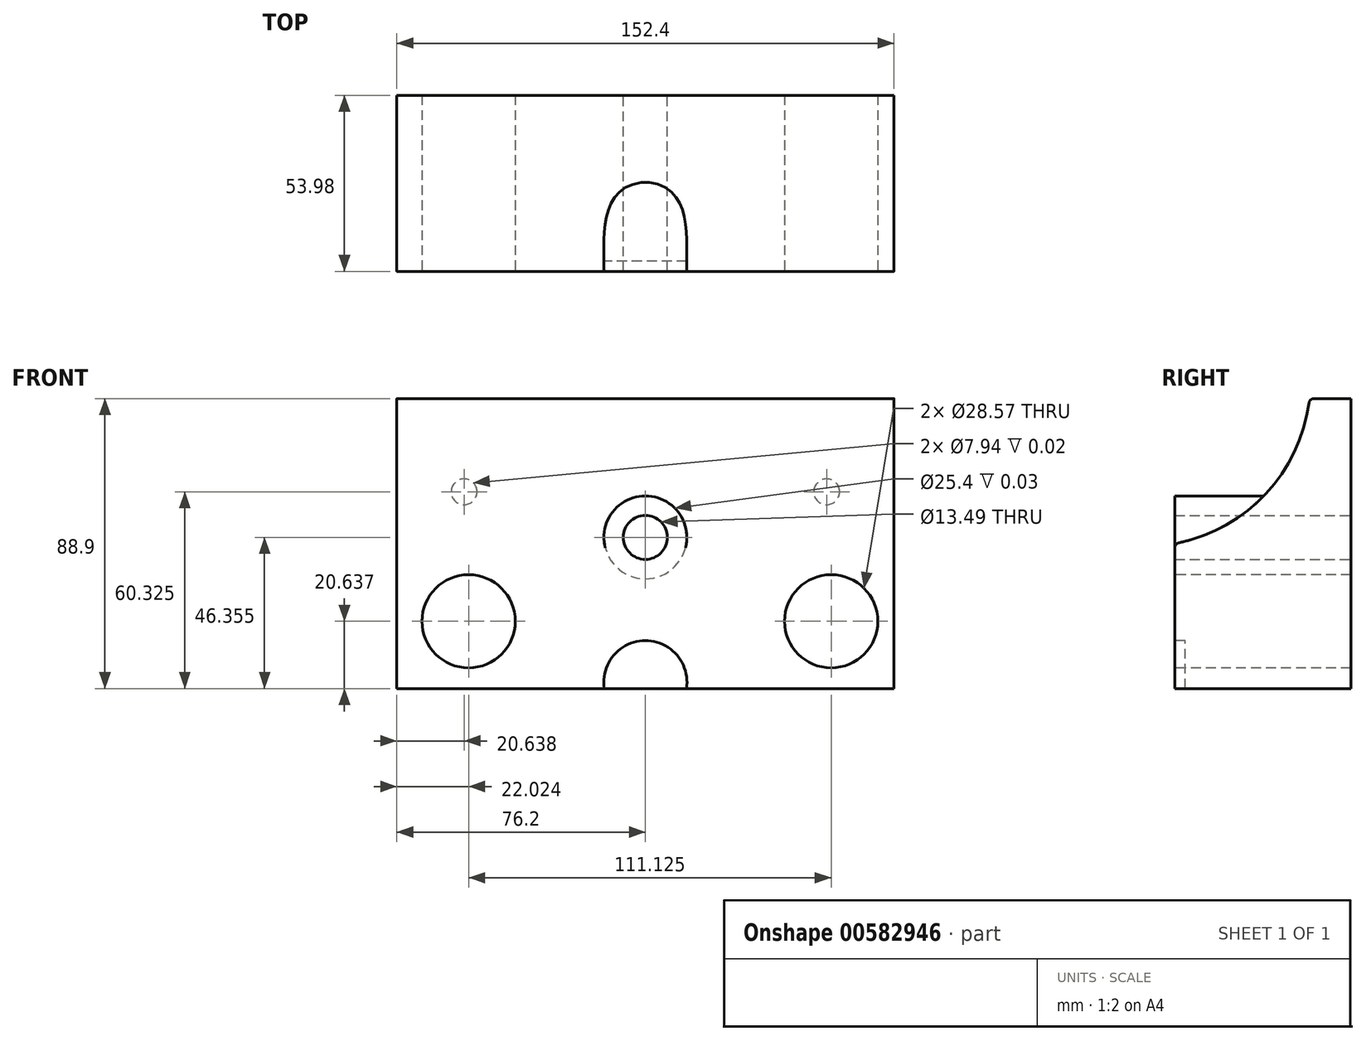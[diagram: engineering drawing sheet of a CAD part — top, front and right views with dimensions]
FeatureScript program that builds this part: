
annotation { "Feature Type Name" : "Feature", "Feature Type Description" : "" }
export const myFeature = defineFeature(function(context is Context, id is Id, definition is map)
    precondition{}
    {
        {
            var Q0;
            Q0=qCreatedBy(makeId("Right.planeOp"),FACE);
            var sketch = newSketch(context, id + "F0", { "sketchPlane" : qUnion([Q0])});
            skLineSegment(sketch, "E0.bottom", {"start": v(-53.97, 0) * mm, "end": v(0, 0) * mm});
            skLineSegment(sketch, "E0.top", {"start": v(-12.7, 88.9) * mm, "end": v(0, 88.9) * mm});
            skLineSegment(sketch, "E0.left", {"start": v(-53.97, 0) * mm, "end": v(-53.98, 44.45) * mm});
            skLineSegment(sketch, "E0.right", {"start": v(0, 0) * mm, "end": v(0, 88.9) * mm});
            skPoint(sketch, "E0.middle", {"position": v(0, 0) * mm});
            skPoint(sketch, "E1", {"position": v(-53.97, 44.45) * mm});
            skLineSegment(sketch, "E2", {"start": v(-53.97, 44.45) * mm, "end": v(-53.97, 44.45) * mm});
            skPoint(sketch, "E3.orphan", {"position": v(-53.98, 88.9) * mm});
            skPoint(sketch, "E4.visualSharp", {"position": v(-294.66, 0) * mm});
            skArc(sketch, "E4.filletArc", {"start": v(-53.97, 44.45) * mm, "mid": v(-25.97, 59.84) * mm, "end": v(-12.7, 88.9) * mm});
            skSolve(sketch);
        }
        {
            var Q0;
            {var subQ1=sQuery(id+"F0.wireOp",EDGE,"E0.bottom");Q0=makeQuery(id+"F0.imprint","IMPRINT",FACE,{"disambiguationData":[TD([[makeQuery(id+"F0.imprint","IMPRINT",EDGE,{"derivedFrom":subQ1}),1.0]])]});}
            extrude(context, id + "F1", {"entities" : qUnion([Q0]), "oppositeDirection" : true, "depth" : 152.4 * mm, "offsetDistance" : 25.4 * mm});
        }
        {
            var Q0;
            Q0=makeQuery(id+"F1.opExtrude","SWEPT_FACE",FACE,{"disambiguationData":[OSD([sQuery(id+"F0.wireOp",EDGE,"E0.left")])]});
            var sketch = newSketch(context, id + "F2", { "sketchPlane" : qUnion([Q0])});
            skPoint(sketch, "E5", {"position": v(-130.38, 20.64) * mm});
            skPoint(sketch, "E6", {"position": v(-19.25, 20.64) * mm});
            skCircle(sketch, "E7", {"center": v(-130.38, 20.64) * mm, "radius": 14.29 * mm});
            skCircle(sketch, "E8", {"center": v(-19.25, 20.64) * mm, "radius": 14.29 * mm});
            skSolve(sketch);
        }
        {
            var Q0;
            Q0=makeQuery(id+"F2.imprint","IMPRINT",FACE,{"disambiguationData":[TD([[makeQuery(id+"F2.imprint","IMPRINT",EDGE,{"derivedFrom":sQuery(id+"F2.wireOp",EDGE,"E7")}),1.0]])]});
            var Q1;
            Q1=makeQuery(id+"F2.imprint","IMPRINT",FACE,{"disambiguationData":[TD([[makeQuery(id+"F2.imprint","IMPRINT",EDGE,{"derivedFrom":sQuery(id+"F2.wireOp",EDGE,"E8")}),1.0]])]});
            extrude(context, id + "F3", {"entities" : qUnion([Q0, Q1]), "operationType" : NewBodyOperationType.REMOVE, "oppositeDirection" : true, "depth" : 101.6 * mm, "offsetDistance" : 25.4 * mm});
        }
        {
            var Q0;
            Q0=makeQuery(id+"F1.opExtrude","SWEPT_FACE",FACE,{"disambiguationData":[OSD([sQuery(id+"F0.wireOp",EDGE,"E0.right")])]});
            var sketch = newSketch(context, id + "F4", { "sketchPlane" : qUnion([Q0])});
            skPoint(sketch, "E9", {"position": v(76.2, 46.35) * mm});
            skCircle(sketch, "E10", {"center": v(76.2, 46.35) * mm, "radius": 12.7 * mm});
            skCircle(sketch, "E11", {"center": v(76.2, 46.35) * mm, "radius": 6.75 * mm});
            skSolve(sketch);
        }
        {
            var Q0;
            Q0 = qSketchRegion(id + "F4", true);
            extrude(context, id + "F5", {"entities" : qUnion([Q0]), "operationType" : NewBodyOperationType.REMOVE, "oppositeDirection" : true, "depth" : 3 / 101.6 * mm, "offsetDistance" : 25.4 * mm});
        }
        {
            var Q0;
            Q0=makeQuery(id+"F5.boolean.opBoolean","SPLIT",FACE,{"disambiguationData":[TD([makeQuery(id+"F5.opExtrude","SWEPT_FACE",FACE,{"disambiguationData":[OSD([sQuery(id+"F4.wireOp",EDGE,"E11")])]})])],"derivedFrom":makeQuery(id+"F1.opExtrude","SWEPT_FACE",FACE,{"disambiguationData":[OSD([sQuery(id+"F0.wireOp",EDGE,"E0.right")])]})});
            extrude(context, id + "F6", {"entities" : qUnion([Q0]), "operationType" : NewBodyOperationType.REMOVE, "oppositeDirection" : true, "depth" : 76.2 * mm, "offsetDistance" : 25.4 * mm});
        }
        {
            var Q0;
            Q0=makeQuery(id+"F5.boolean.opBoolean","COPY",FACE,{"derivedFrom":makeQuery(id+"F5.opExtrude","CAP_FACE",FACE,{"disambiguationData":[OSD([sQuery(id+"F4.wireOp",EDGE,"E10"),sQuery(id+"F4.wireOp",EDGE,"E11")])],"isStart":false})});
            var Q1;
            Q1=makeQuery(id+"F1.opExtrude","SWEPT_FACE",FACE,{"disambiguationData":[OSD([sQuery(id+"F0.wireOp",EDGE,"E0.left")])]});
            extrude(context, id + "F7", {"entities" : qUnion([Q0]), "operationType" : NewBodyOperationType.ADD, "endBound" : BoundingType.UP_TO_SURFACE, "oppositeDirection" : true, "depth" : 33.34 * mm, "endBoundEntityFace" : qUnion([Q1]), "offsetDistance" : 25.4 * mm});
        }
        {
            var Q0;
            Q0=makeQuery(id+"F2.imprint","IMPRINT",FACE,{"disambiguationData":[TD([[makeQuery(id+"F2.imprint","IMPRINT",EDGE,{"derivedFrom":sQuery(id+"F2.wireOp",EDGE,"E7")}),-1.0]])]});
            var sketch = newSketch(context, id + "F8", { "sketchPlane" : qUnion([Q0])});
            skCircle(sketch, "E12", {"center": v(-76.2, 1.9) * mm, "radius": 12.77 * mm});
            skSolve(sketch);
        }
        {
            var Q0;
            Q0 = qSketchRegion(id + "F8", true);
            var Q1;
            Q1=sQuery(id+"F8.wireOp",EDGE,"E12");
            extrude(context, id + "F9", {"entities" : qUnion([Q0]), "operationType" : NewBodyOperationType.REMOVE, "surfaceEntities" : qUnion([Q1]), "oppositeDirection" : true, "depth" : 3.17 * mm, "offsetDistance" : 25.4 * mm});
        }
        {
            var Q0;
            Q0=makeQuery(id+"F1.opExtrude","SWEPT_EDGE",EDGE,{"disambiguationData":[OSD([sQuery(id+"F0.wireOp",EDGE,"E0.top"),sQuery(id+"F0.wireOp",EDGE,"E4.filletArc")])]});
            var Q1;
            {var subQ0=sQuery(id+"F0.wireOp",EDGE,"E4.filletArc");var subQ1=sQuery(id+"F0.wireOp",EDGE,"E0.left");Q1=makeQuery(id+"F6.boolean.opBoolean","SPLIT",EDGE,{"disambiguationData":[TD([makeQuery(id+"F1.opExtrude","CAP_FACE",FACE,{"disambiguationData":[OSD([sQuery(id+"F0.wireOp",EDGE,"E0.bottom"),sQuery(id+"F0.wireOp",EDGE,"E0.top"),subQ1,sQuery(id+"F0.wireOp",EDGE,"E0.right"),subQ0])],"isStart":false})])],"derivedFrom":makeQuery(id+"F1.opExtrude","SWEPT_EDGE",EDGE,{"disambiguationData":[OSD([subQ1,subQ0])]})});}
            var Q2;
            {var subQ0=sQuery(id+"F0.wireOp",EDGE,"E4.filletArc");var subQ1=sQuery(id+"F0.wireOp",EDGE,"E0.left");Q2=makeQuery(id+"F6.boolean.opBoolean","SPLIT",EDGE,{"disambiguationData":[TD([makeQuery(id+"F1.opExtrude","CAP_FACE",FACE,{"disambiguationData":[OSD([sQuery(id+"F0.wireOp",EDGE,"E0.bottom"),sQuery(id+"F0.wireOp",EDGE,"E0.top"),subQ1,sQuery(id+"F0.wireOp",EDGE,"E0.right"),subQ0])],"isStart":true})])],"derivedFrom":makeQuery(id+"F1.opExtrude","SWEPT_EDGE",EDGE,{"disambiguationData":[OSD([subQ1,subQ0])]})});}
            fillet(context, id + "F10", {"entities" : qUnion([Q0, Q1, Q2]), "radius" : 1.59 * mm, "tangentPropagation" : true, "allowEdgeOverflow" : false});
        }
        {
            var Q0;
            {var subQ2=sQuery(id+"F0.wireOp",EDGE,"E0.right");var subQ4=sQuery(id+"F0.wireOp",EDGE,"E0.bottom");Q0=makeQuery(id+"F5.boolean.opBoolean","SPLIT",FACE,{"disambiguationData":[TD([makeQuery(id+"F1.opExtrude","SWEPT_FACE",FACE,{"disambiguationData":[OSD([subQ4])]})])],"derivedFrom":makeQuery(id+"F1.opExtrude","SWEPT_FACE",FACE,{"disambiguationData":[OSD([subQ2])]})});}
            var sketch = newSketch(context, id + "F11", { "sketchPlane" : qUnion([Q0])});
            skCircle(sketch, "E13", {"center": v(20.64, 60.33) * mm, "radius": 3.97 * mm});
            skCircle(sketch, "E14", {"center": v(131.76, 60.33) * mm, "radius": 3.97 * mm});
            skSolve(sketch);
        }
        {
            var Q0;
            Q0=makeQuery(id+"F11.imprint","IMPRINT",FACE,{"disambiguationData":[TD([[makeQuery(id+"F11.imprint","IMPRINT",EDGE,{"derivedFrom":sQuery(id+"F11.wireOp",EDGE,"E13")}),1.0]])]});
            var Q1;
            Q1=makeQuery(id+"F11.imprint","IMPRINT",FACE,{"disambiguationData":[TD([[makeQuery(id+"F11.imprint","IMPRINT",EDGE,{"derivedFrom":sQuery(id+"F11.wireOp",EDGE,"E14")}),1.0]])]});
            extrude(context, id + "F12", {"entities" : qUnion([Q0, Q1]), "operationType" : NewBodyOperationType.REMOVE, "oppositeDirection" : true, "depth" : 1 / 50.8 * mm, "offsetDistance" : 25.4 * mm});
        }
    });
